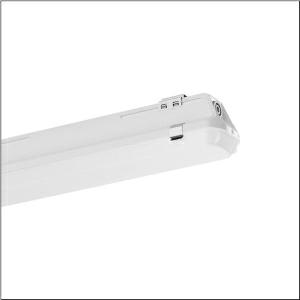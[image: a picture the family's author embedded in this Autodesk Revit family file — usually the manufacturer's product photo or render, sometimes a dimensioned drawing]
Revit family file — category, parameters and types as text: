
# Revit family: monsun_r__21_51fb107p460b005_4f74
name_source: partatom
category: Lighting Fixtures
units: mm (PartAtom-declared; Revit-internal decimal feet)

## family parameters
Cut with Voids When Loaded = No
Host = Face
Light Source = No
Part Type = Normal
Room Calculation Point = No
Round Connector Dimension = Use Diameter
Shared = No

## types (1)
- Monsun® 21 (1 x LED, 6000 lm, 38 W, 4000K)
    Apparent Load = 38 VA
    CIE Flux Codes = 47 77 93 94 100
    Color Rendering = 80
    Color Temperature = 4000K
    Default Elevation = 1800 mm
    Description = Monsun® 21, damp-proof luminaire, chain hanger, primary optical cover: enclosure, of PMMA, light emission: direct distribution, primary light characteristic: symmetric, installation type: suspended mounting, surface-mounted, horizontal mounting, vertical mounting, LED, rated luminous flux: 6.000lm, luminous efficacy: 158lm/W, light colour: 840, colour temperature: 4000K, control gear: ECG, with terminal, 3-pole, max. 2.5mm², through-wiring: 5x 2.5mm², mains connection: 220..240V, AC, 50/60Hz, rated input power: 38W, housing, of glass-fibre reinforced polyester, uncoated, bright grey, incl. chain hanger, length: 1.590mm, width: 90mm, height: 88mm, clip for enclosure, of stainless steel (V2A), ceiling mounting element, of stainless steel (V2A), chain hanger, of stainless steel (V2A), protection rating (complete): IP66, insulation class (complete): insulation class I (protective earthing), certification: CE, ENEC, VDE, UKCA, protection symbol: D, impact resistance: IK04, permissible operating ambient temperature: -25..+35°C, standard: EN 50419, EN 60598-2-1, corresponds to IFS (International Featured Standards) requirements for safety and quality in the food industry, for indoor or canopied outdoor use, no direct snow, no direct sun, no direct rain, contact your sales advisor before using the luminaires in applications with unclear chemical exposure, large temperature fluctuations or condensation-forming humidity, LABS conformity tested according to VDMA 24364:2018-05, packaging unit: 1 piece
    Height = 89 mm
    Lamp = 1 x LED
    Lamp Light Flux = 6000 lm
    Lamp Power = 38 W
    Lamp count = 1
    Length = 1590 mm
    Luminous efficacy = 158 lm/W
    Manufacturer = Siteco
    ModVariant = No
    Model = 51FB107P460B005
    Mounting Place = Ceiling
    Mounting Type = Surface mounted
    Number of Poles = 1
    OnlyDefault = Yes
    Power Factor = 1
    Product Name = Monsun® 21
    Product group = damp-proof luminaire
    ProductGroupID = 300
    Protection Class = Protection class I
    Protection Degree = IP 66
    RLX_Detail_Level = 1
    RLX_Emergency_Light_Flux = 0 lm
    RLX_Emergency_Type = 0
    RLX_Emergency_Type_DB = No
    RlxData = <blob elided: 88917 chars, md5=0e47d7b5>
    Socket = socket
    Standby Power = 0 W
    System Light Flux = 6000 lm
    System Power = 38 W
    Type Comments = Product without accessories
    Type Image = l_1006717.jpg
    URL = http://relux.com
    VarID = ---
    Voltage = 0 V
    Weight = 0.00 kg
    Width = 90 mm

## geometry (parser evidence)
native form markers: Blend x4, Sweep x13
no freeform markers — native parametric forms only
